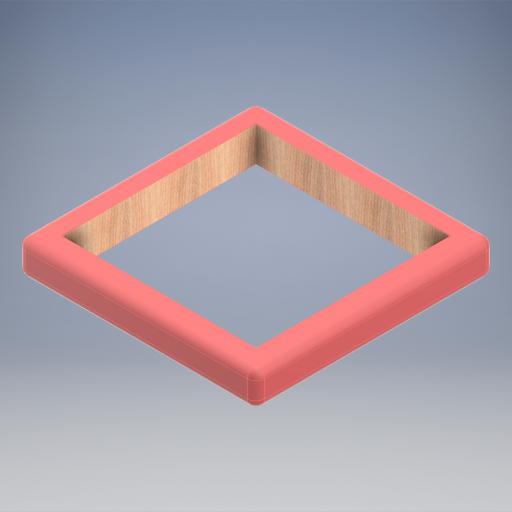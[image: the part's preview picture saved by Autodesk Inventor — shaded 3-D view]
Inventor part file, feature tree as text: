
AUTODESK INVENTOR PART (.ipt)
format: ipt  version: 2024.2 (Build 282272000, 272)  size: 366,592 bytes
history: native  units: in
note: dims shown in document units (in); Inventor stores cm internally (conversion verified against a paired STEP export)
features: extrude x5, fillet x1, other x1
ambient origin geometry x8: Origin, YZ Plane, XZ Plane, XY Plane, X Axis, Y Axis, Z Axis, Center Point
bodies: Solid1 (feature_tree)
feature tree (7):
  extrude  "Extrusion1"  Depth=3.25in
  fillet  "Fillet1"  Radius=3.25in
  other  "Bumper_Gaps"
  extrude  "Front_Gap"  Depth=28.0in
  extrude  "Back_Gap"  Depth=28.0in
  extrude  "Left_Gap"  Depth=5.0in TaperAngle=0.0deg
  extrude  "Right_Gap"  Depth=1.25in
